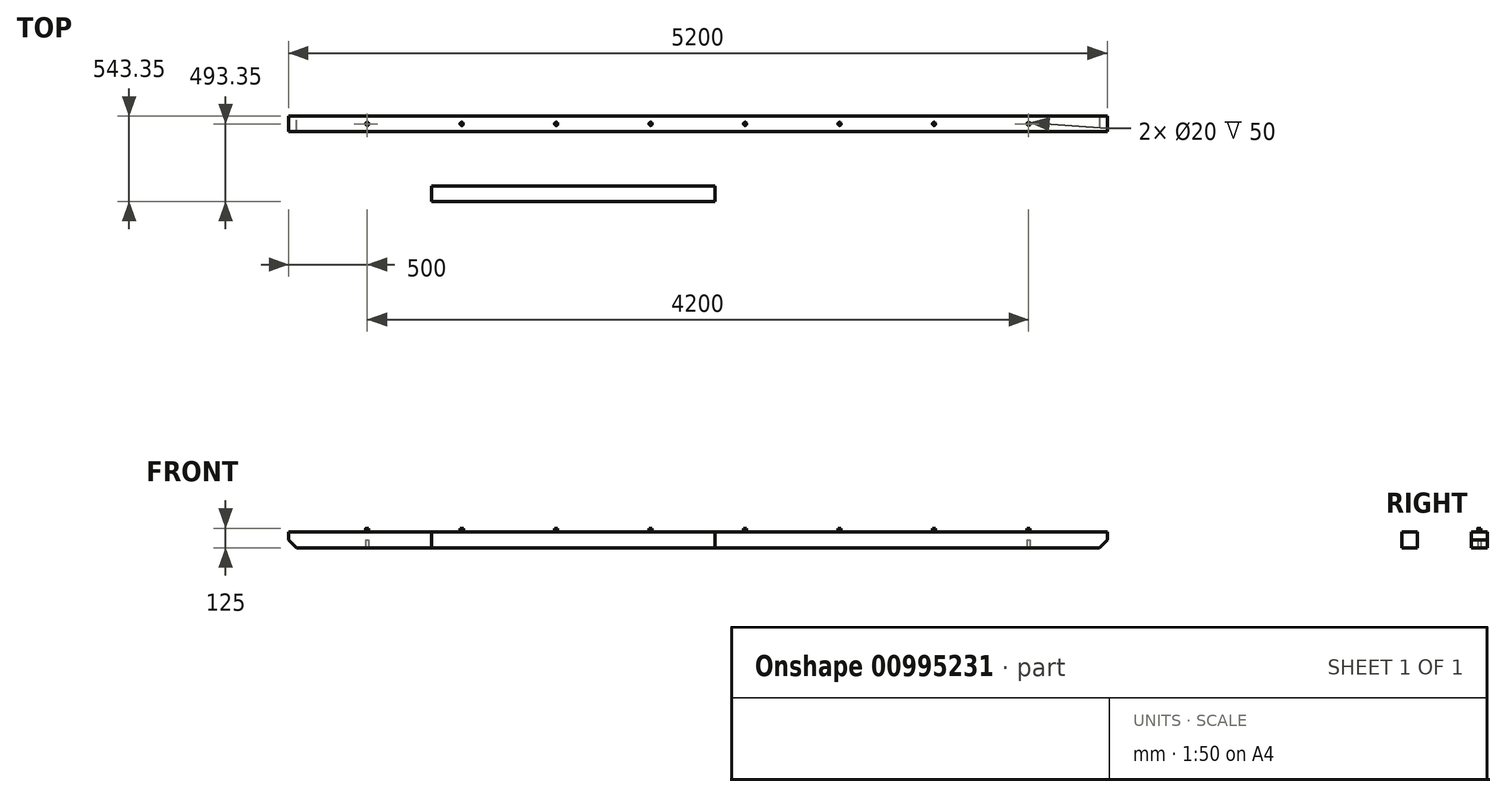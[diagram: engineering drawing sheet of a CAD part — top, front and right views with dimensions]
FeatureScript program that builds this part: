
annotation { "Feature Type Name" : "Feature", "Feature Type Description" : "" }
export const myFeature = defineFeature(function(context is Context, id is Id, definition is map)
    precondition{}
    {
        {
            var Q0;
            Q0=qCreatedBy(makeId("Top.planeOp"),FACE);
            var sketch = newSketch(context, id + "F0", { "sketchPlane" : qUnion([Q0])});
            skLineSegment(sketch, "E0.bottom", {"start": v(2600, -50) * mm, "end": v(-2600, -50) * mm});
            skLineSegment(sketch, "E0.top", {"start": v(2600, 50) * mm, "end": v(-2600, 50) * mm});
            skLineSegment(sketch, "E0.left", {"start": v(2600, -50) * mm, "end": v(2600, 50) * mm});
            skLineSegment(sketch, "E0.right", {"start": v(-2600, -50) * mm, "end": v(-2600, 50) * mm});
            skPoint(sketch, "E0.middle", {"position": v(0, 0) * mm});
            skLineSegment(sketch, "E1.bottom", {"start": v(-1692.88, -393.35) * mm, "end": v(107.12, -393.35) * mm});
            skLineSegment(sketch, "E1.top", {"start": v(-1692.88, -493.35) * mm, "end": v(107.12, -493.35) * mm});
            skLineSegment(sketch, "E1.left", {"start": v(-1692.88, -393.35) * mm, "end": v(-1692.88, -493.35) * mm});
            skLineSegment(sketch, "E1.right", {"start": v(107.12, -393.35) * mm, "end": v(107.12, -493.35) * mm});
            skSolve(sketch);
        }
        {
            var Q0;
            Q0=makeQuery(id+"F0.imprint","IMPRINT",FACE,{"disambiguationData":[TD([[makeQuery(id+"F0.imprint","IMPRINT",EDGE,{"derivedFrom":sQuery(id+"F0.wireOp",EDGE,"E0.bottom")}),-1.0]])]});
            var Q1;
            Q1=makeQuery(id+"F0.imprint","IMPRINT",FACE,{"disambiguationData":[TD([[makeQuery(id+"F0.imprint","IMPRINT",EDGE,{"derivedFrom":sQuery(id+"F0.wireOp",EDGE,"E1.bottom")}),-1.0]])]});
            extrude(context, id + "F1", {"entities" : qUnion([Q0, Q1]), "depth" : 100 * mm, "offsetDistance" : 25 * mm});
        }
        {
            var Q0;
            Q0=makeQuery(id+"F1.opExtrude","CAP_FACE",FACE,{"disambiguationData":[OSD([sQuery(id+"F0.wireOp",EDGE,"E0.bottom"),sQuery(id+"F0.wireOp",EDGE,"E0.top"),sQuery(id+"F0.wireOp",EDGE,"E0.left"),sQuery(id+"F0.wireOp",EDGE,"E0.right")])],"isStart":true});
            var sketch = newSketch(context, id + "F2", { "sketchPlane" : qUnion([Q0])});
            skPoint(sketch, "E2.centerSnap0", {"position": v(-2600, 0) * mm});
            skCircle(sketch, "E3", {"center": v(-2100, 0) * mm, "radius": 10 * mm});
            skLineSegment(sketch, "E4", {"start": v(-2100, 0) * mm, "end": v(2100, 0) * mm, "construction": true});
            skLineSegment(sketch, "E5", {"start": v(0, 167.87) * mm, "end": v(0, -224.3) * mm, "construction": true});
            skPoint(sketch, "E5.startSnap0", {"position": v(0, 0) * mm});
            skCircle(sketch, "E6", {"center": v(2100, 0) * mm, "radius": 10 * mm});
            skSolve(sketch);
        }
        {
            var Q0;
            Q0 = qSketchRegion(id + "F2", true);
            extrude(context, id + "F3", {"entities" : qUnion([Q0]), "operationType" : NewBodyOperationType.REMOVE, "oppositeDirection" : true, "depth" : 50 * mm, "offsetDistance" : 25 * mm});
        }
        {
            var Q0;
            Q0=makeQuery(id+"F1.opExtrude","CAP_FACE",FACE,{"disambiguationData":[OSD([sQuery(id+"F0.wireOp",EDGE,"E0.bottom"),sQuery(id+"F0.wireOp",EDGE,"E0.top"),sQuery(id+"F0.wireOp",EDGE,"E0.left"),sQuery(id+"F0.wireOp",EDGE,"E0.right")])],"isStart":false});
            var sketch = newSketch(context, id + "F4", { "sketchPlane" : qUnion([Q0])});
            skCircle(sketch, "E7", {"center": v(1500, 0) * mm, "radius": 10 * mm});
            skCircle(sketch, "E8", {"center": v(900, 0) * mm, "radius": 10 * mm});
            skCircle(sketch, "E9", {"center": v(300, 0) * mm, "radius": 10 * mm});
            skCircle(sketch, "E10", {"center": v(-300, 0) * mm, "radius": 10 * mm});
            skCircle(sketch, "E11", {"center": v(-900, 0) * mm, "radius": 10 * mm});
            skCircle(sketch, "E12", {"center": v(-1500, 0) * mm, "radius": 10 * mm});
            skCircle(sketch, "E13", {"center": v(-2100, 0) * mm, "radius": 10 * mm});
            skCircle(sketch, "E14", {"center": v(2100, 0) * mm, "radius": 10 * mm});
            skSolve(sketch);
        }
        {
            var Q0;
            Q0=makeQuery(id+"F4.imprint","IMPRINT",FACE,{"disambiguationData":[TD([[makeQuery(id+"F4.imprint","IMPRINT",EDGE,{"derivedFrom":sQuery(id+"F4.wireOp",EDGE,"E13")}),1.0]])]});
            var Q1;
            Q1=makeQuery(id+"F4.imprint","IMPRINT",FACE,{"disambiguationData":[TD([[makeQuery(id+"F4.imprint","IMPRINT",EDGE,{"derivedFrom":sQuery(id+"F4.wireOp",EDGE,"E12")}),1.0]])]});
            var Q2;
            Q2=makeQuery(id+"F4.imprint","IMPRINT",FACE,{"disambiguationData":[TD([[makeQuery(id+"F4.imprint","IMPRINT",EDGE,{"derivedFrom":sQuery(id+"F4.wireOp",EDGE,"E11")}),1.0]])]});
            var Q3;
            Q3=makeQuery(id+"F4.imprint","IMPRINT",FACE,{"disambiguationData":[TD([[makeQuery(id+"F4.imprint","IMPRINT",EDGE,{"derivedFrom":sQuery(id+"F4.wireOp",EDGE,"E10")}),1.0]])]});
            var Q4;
            Q4=makeQuery(id+"F4.imprint","IMPRINT",FACE,{"disambiguationData":[TD([[makeQuery(id+"F4.imprint","IMPRINT",EDGE,{"derivedFrom":sQuery(id+"F4.wireOp",EDGE,"E9")}),1.0]])]});
            var Q5;
            Q5=makeQuery(id+"F4.imprint","IMPRINT",FACE,{"disambiguationData":[TD([[makeQuery(id+"F4.imprint","IMPRINT",EDGE,{"derivedFrom":sQuery(id+"F4.wireOp",EDGE,"E8")}),1.0]])]});
            var Q6;
            Q6=makeQuery(id+"F4.imprint","IMPRINT",FACE,{"disambiguationData":[TD([[makeQuery(id+"F4.imprint","IMPRINT",EDGE,{"derivedFrom":sQuery(id+"F4.wireOp",EDGE,"E7")}),1.0]])]});
            var Q7;
            Q7=makeQuery(id+"F4.imprint","IMPRINT",FACE,{"disambiguationData":[TD([[makeQuery(id+"F4.imprint","IMPRINT",EDGE,{"derivedFrom":sQuery(id+"F4.wireOp",EDGE,"E7")}),1.0]])]});
            var Q8;
            Q8=makeQuery(id+"F4.imprint","IMPRINT",FACE,{"disambiguationData":[TD([[makeQuery(id+"F4.imprint","IMPRINT",EDGE,{"derivedFrom":sQuery(id+"F4.wireOp",EDGE,"E14")}),1.0]])]});
            extrude(context, id + "F5", {"entities" : qUnion([Q0, Q1, Q2, Q3, Q4, Q5, Q6, Q7, Q8]), "operationType" : NewBodyOperationType.ADD, "depth" : 25 * mm, "offsetDistance" : 25 * mm});
        }
        {
            var Q0;
            Q0=makeQuery(id+"F1.opExtrude","CAP_EDGE",EDGE,{"disambiguationData":[OSD([sQuery(id+"F0.wireOp",EDGE,"E0.right")])],"isStart":true});
            var Q1;
            Q1=makeQuery(id+"F1.opExtrude","CAP_EDGE",EDGE,{"disambiguationData":[OSD([sQuery(id+"F0.wireOp",EDGE,"E0.left")])],"isStart":true});
            chamfer(context, id + "F6", {"entities" : qUnion([Q0, Q1]), "width" : 50 * mm, "tangentPropagation" : true});
        }
    });
